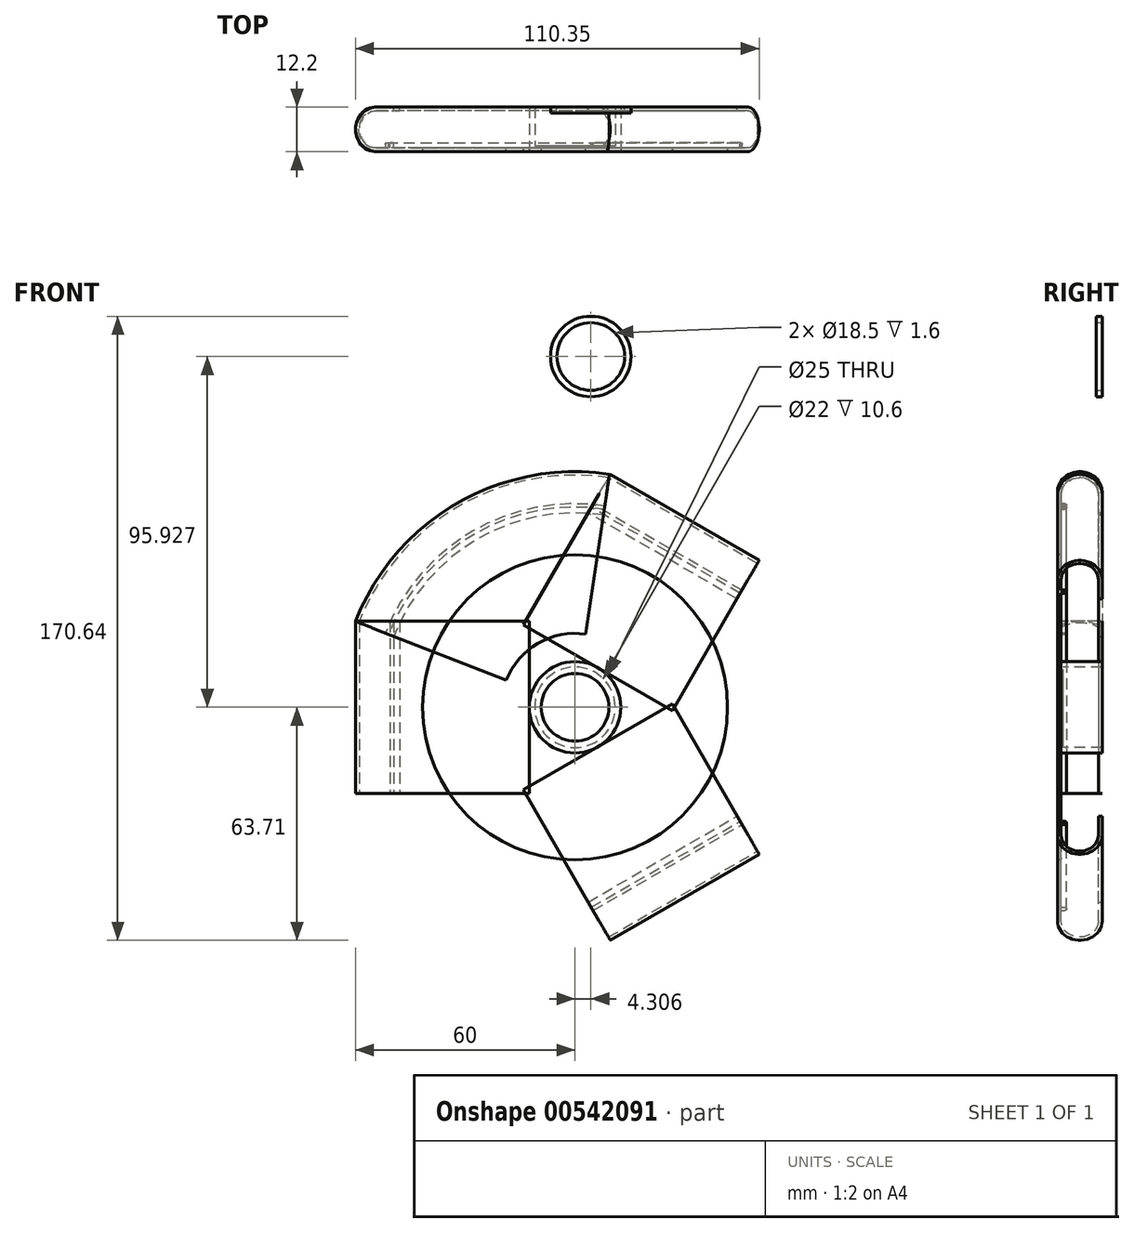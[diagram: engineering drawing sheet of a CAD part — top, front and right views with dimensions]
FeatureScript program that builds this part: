
annotation { "Feature Type Name" : "Feature", "Feature Type Description" : "" }
export const myFeature = defineFeature(function(context is Context, id is Id, definition is map)
    precondition{}
    {
        {
            var Q0;
            Q0=qCreatedBy(makeId("Front.planeOp"),FACE);
            var sketch = newSketch(context, id + "F0", { "sketchPlane" : qUnion([Q0])});
            skCircle(sketch, "E0", {"center": v(0, 0) * mm, "radius": 11 * mm});
            skCircle(sketch, "E1", {"center": v(0, 0) * mm, "radius": 12.5 * mm});
            skLineSegment(sketch, "E2.0", {"start": v(9.65, 63.71) * mm, "end": v(50.35, 40.21) * mm});
            skLineSegment(sketch, "E2.2", {"start": v(50.35, -40.21) * mm, "end": v(9.65, -63.71) * mm});
            skLineSegment(sketch, "E2.4", {"start": v(-60, -23.5) * mm, "end": v(-60, 23.5) * mm});
            skLineSegment(sketch, "E3", {"start": v(-6.25, -10.83) * mm, "end": v(-34.64, -60) * mm, "construction": true});
            skLineSegment(sketch, "E4", {"start": v(12.5, 0) * mm, "end": v(69.28, 0) * mm, "construction": true});
            skLineSegment(sketch, "E5", {"start": v(-6.25, 10.83) * mm, "end": v(-34.64, 60) * mm, "construction": true});
            skPoint(sketch, "E6", {"position": v(30, -51.96) * mm});
            skPoint(sketch, "E7", {"position": v(9.65, -63.71) * mm});
            skPoint(sketch, "E8", {"position": v(50.35, -40.21) * mm});
            skPoint(sketch, "E9", {"position": v(30, 51.96) * mm});
            skPoint(sketch, "E10", {"position": v(9.65, 63.71) * mm});
            skPoint(sketch, "E11", {"position": v(50.35, 40.21) * mm});
            skPoint(sketch, "E12", {"position": v(-60, 0) * mm});
            skPoint(sketch, "E13", {"position": v(-60, 23.5) * mm});
            skPoint(sketch, "E14", {"position": v(-60, -23.5) * mm});
            skLineSegment(sketch, "E15", {"start": v(0, 0) * mm, "end": v(4.62, 8.01) * mm, "construction": true});
            skLineSegment(sketch, "E16", {"start": v(0, 0) * mm, "end": v(-9.25, 0) * mm, "construction": true});
            skLineSegment(sketch, "E17", {"start": v(0, 0) * mm, "end": v(4.62, -8.01) * mm, "construction": true});
            skLineSegment(sketch, "E18", {"start": v(0, 0) * mm, "end": v(1.39, 9.15) * mm, "construction": true});
            skLineSegment(sketch, "E19", {"start": v(0, 0) * mm, "end": v(7.23, 5.77) * mm, "construction": true});
            skLineSegment(sketch, "E20", {"start": v(0, 0) * mm, "end": v(-8.61, 3.37) * mm, "construction": true});
            skLineSegment(sketch, "E21", {"start": v(0, 0) * mm, "end": v(-8.61, -3.37) * mm, "construction": true});
            skLineSegment(sketch, "E22", {"start": v(0, 0) * mm, "end": v(1.39, -9.15) * mm, "construction": true});
            skLineSegment(sketch, "E23", {"start": v(0, 0) * mm, "end": v(7.23, -5.77) * mm, "construction": true});
            skCircle(sketch, "E24", {"center": v(0, 0) * mm, "radius": 9.25 * mm});
            skLineSegment(sketch, "E25.trimOffspring", {"start": v(5.5, 9.53) * mm, "end": v(6.25, 10.83) * mm, "construction": true});
            skLineSegment(sketch, "E26.trimOffspring", {"start": v(1.65, 10.88) * mm, "end": v(9.65, 63.71) * mm, "construction": true});
            skLineSegment(sketch, "E27.trimOffspring", {"start": v(8.6, 6.86) * mm, "end": v(50.35, 40.21) * mm, "construction": true});
            skLineSegment(sketch, "E28.trimOffspring", {"start": v(8.6, -6.86) * mm, "end": v(50.35, -40.21) * mm, "construction": true});
            skLineSegment(sketch, "E29.trimOffspring", {"start": v(5.5, -9.53) * mm, "end": v(6.25, -10.83) * mm, "construction": true});
            skLineSegment(sketch, "E30.trimOffspring", {"start": v(1.65, -10.88) * mm, "end": v(9.65, -63.71) * mm, "construction": true});
            skLineSegment(sketch, "E31.trimOffspring", {"start": v(-10.24, -4.01) * mm, "end": v(-60, -23.5) * mm, "construction": true});
            skLineSegment(sketch, "E32.trimOffspring", {"start": v(-11, 0) * mm, "end": v(-12.5, 0) * mm, "construction": true});
            skLineSegment(sketch, "E33.trimOffspring", {"start": v(-10.24, 4.01) * mm, "end": v(-60, 23.5) * mm, "construction": true});
            skCircle(sketch, "E34", {"center": v(0, 0) * mm, "radius": 20.56 * mm});
            skCircle(sketch, "E35", {"center": v(0, 0) * mm, "radius": 41.68 * mm});
            skSolve(sketch);
        }
        {
            var Q0;
            Q0=makeQuery(id+"F0.imprint","IMPRINT",FACE,{"disambiguationData":[TD([[makeQuery(id+"F0.imprint","IMPRINT",EDGE,{"derivedFrom":sQuery(id+"F0.wireOp",EDGE,"E0")}),-1.0]])]});
            extrude(context, id + "F1", {"entities" : qUnion([Q0]), "oppositeDirection" : true, "depth" : 12.2 * mm, "offsetDistance" : 25 * mm});
        }
        {
            var Q0;
            Q0=qCreatedBy(makeId("Top.planeOp"),FACE);
            var sketch = newSketch(context, id + "F2", { "sketchPlane" : qUnion([Q0])});
            skArc(sketch, "E36", {"start": v(-53.9, 11.2) * mm, "mid": v(-59, 6.1) * mm, "end": v(-53.9, 1) * mm});
            skArc(sketch, "E37", {"start": v(-53.9, 12.2) * mm, "mid": v(-60, 6.1) * mm, "end": v(-53.9, 0) * mm});
            skLineSegment(sketch, "E38", {"start": v(-53.9, 6.1) * mm, "end": v(-53.9, 11.2) * mm, "construction": true});
            skLineSegment(sketch, "E39", {"start": v(-53.9, 6.1) * mm, "end": v(-53.9, 1) * mm, "construction": true});
            skLineSegment(sketch, "E40", {"start": v(-53.9, 0) * mm, "end": v(-49.58, 0) * mm});
            skLineSegment(sketch, "E41", {"start": v(-53.9, 1) * mm, "end": v(-50.58, 1) * mm});
            skPoint(sketch, "E42", {"position": v(-50.58, 1) * mm});
            skLineSegment(sketch, "E43.left", {"start": v(-50.58, 1) * mm, "end": v(-50.58, 2) * mm});
            skLineSegment(sketch, "E43.right", {"start": v(-49.58, 1) * mm, "end": v(-49.58, 2) * mm});
            skCircle(sketch, "E44", {"center": v(-53.9, 6.1) * mm, "radius": 5.1 * mm, "construction": true});
            skArc(sketch, "E45", {"start": v(-49.58, 2) * mm, "mid": v(-50.08, 2.5) * mm, "end": v(-50.58, 2) * mm});
            skLineSegment(sketch, "E46", {"start": v(0, 1) * mm, "end": v(0, 26.09) * mm, "construction": true});
            skLineSegment(sketch, "E47", {"start": v(0, 0) * mm, "end": v(0, -37.62) * mm, "construction": true});
            skPoint(sketch, "E48", {"position": v(-49.58, 1) * mm});
            skPoint(sketch, "E49", {"position": v(-49.58, 0) * mm});
            skLineSegment(sketch, "E50", {"start": v(0, 0) * mm, "end": v(-49.58, 0) * mm});
            skLineSegment(sketch, "E51", {"start": v(-49.58, 1) * mm, "end": v(-12.5, 1) * mm});
            skLineSegment(sketch, "E52", {"start": v(0, 1) * mm, "end": v(0, 0) * mm});
            skLineSegment(sketch, "E53", {"start": v(-53.9, 11.2) * mm, "end": v(-47.9, 11.2) * mm});
            skLineSegment(sketch, "E54", {"start": v(-47.9, 11.2) * mm, "end": v(-47.9, 12.2) * mm});
            skLineSegment(sketch, "E55", {"start": v(-47.9, 12.2) * mm, "end": v(-53.9, 12.2) * mm});
            skPoint(sketch, "E56.start.orphan", {"position": v(-60, 6.1) * mm});
            skLineSegment(sketch, "E57.0", {"start": v(12.5, 0) * mm, "end": v(-12.5, 0) * mm});
            skLineSegment(sketch, "E58", {"start": v(-53.9, 0) * mm, "end": v(-12.5, 0) * mm});
            skPoint(sketch, "E59", {"position": v(-12.5, 1) * mm});
            skPoint(sketch, "E60", {"position": v(-12.5, 0) * mm});
            skLineSegment(sketch, "E61", {"start": v(-12.5, 0) * mm, "end": v(-12.5, 1) * mm});
            skSolve(sketch);
        }
        {
            var Q0;
            Q0=makeQuery(id+"F2.imprint","IMPRINT",FACE,{"disambiguationData":[TD([[makeQuery(id+"F2.imprint","IMPRINT",EDGE,{"derivedFrom":sQuery(id+"F2.wireOp",EDGE,"E36")}),-1.0]])]});
            extrude(context, id + "F3", {"entities" : qUnion([Q0]), "endBound" : BoundingType.SYMMETRIC, "depth" : 47 * mm, "offsetDistance" : 25 * mm});
        }
        {
            var Q0;
            Q0=sQuery(id+"F0.wireOp",EDGE,"E2.2");
            cPoint(context, id + "F4", {"entities" : qUnion([Q0]), "parameter" : 0.5});
        }
        {
            var Q0;
            Q0=sQuery(id+"F0.wireOp",EDGE,"E2.2");
            var Q1;
            Q1=qCreatedBy(id+"F4",VERTEX);
            cPlane(context, id + "F5", {"entities" : qUnion([Q0, Q1]), "cplaneType" : CPlaneType.LINE_POINT, "offset" : 25 * mm, "width" : 150 * mm, "height" : 150 * mm});
        }
        {
            var Q0;
            Q0=qCreatedBy(id+"F5.planeOp",FACE);
            var sketch = newSketch(context, id + "F6", { "sketchPlane" : qUnion([Q0])});
            skArc(sketch, "E62", {"start": v(-11.2, -53.9) * mm, "mid": v(-6.1, -59) * mm, "end": v(-1, -53.9) * mm});
            skArc(sketch, "E63", {"start": v(-12.2, -53.9) * mm, "mid": v(-6.1, -60) * mm, "end": v(0, -53.9) * mm});
            skLineSegment(sketch, "E64", {"start": v(-6.1, -53.9) * mm, "end": v(-11.2, -53.9) * mm, "construction": true});
            skLineSegment(sketch, "E65", {"start": v(-6.1, -53.9) * mm, "end": v(-1, -53.9) * mm, "construction": true});
            skLineSegment(sketch, "E66", {"start": v(0, -53.9) * mm, "end": v(0, -49.58) * mm});
            skLineSegment(sketch, "E67", {"start": v(-1, -53.9) * mm, "end": v(-1, -50.58) * mm});
            skPoint(sketch, "E68", {"position": v(-1, -50.58) * mm});
            skLineSegment(sketch, "E69.left", {"start": v(-1, -50.58) * mm, "end": v(-2, -50.58) * mm});
            skLineSegment(sketch, "E69.right", {"start": v(-1, -49.58) * mm, "end": v(-2, -49.58) * mm});
            skCircle(sketch, "E70", {"center": v(-6.1, -53.9) * mm, "radius": 5.1 * mm, "construction": true});
            skArc(sketch, "E71", {"start": v(-2, -49.58) * mm, "mid": v(-2.5, -50.08) * mm, "end": v(-2, -50.58) * mm});
            skPoint(sketch, "E72", {"position": v(-1, -49.58) * mm});
            skPoint(sketch, "E73", {"position": v(0, -49.58) * mm});
            skLineSegment(sketch, "E74", {"start": v(0, 0) * mm, "end": v(0, -49.58) * mm});
            skLineSegment(sketch, "E75", {"start": v(-1, -49.58) * mm, "end": v(-1, -12.5) * mm});
            skLineSegment(sketch, "E76", {"start": v(-11.2, -53.9) * mm, "end": v(-11.2, -47.9) * mm});
            skLineSegment(sketch, "E77", {"start": v(-11.2, -47.9) * mm, "end": v(-12.2, -47.9) * mm});
            skLineSegment(sketch, "E78", {"start": v(-12.2, -47.9) * mm, "end": v(-12.2, -53.9) * mm});
            skPoint(sketch, "E79.start.orphan", {"position": v(-6.1, -60) * mm});
            skLineSegment(sketch, "E80", {"start": v(-1, -12.5) * mm, "end": v(0, -12.5) * mm});
            skSolve(sketch);
        }
        {
            var Q0;
            Q0=makeQuery(id+"F6.imprint","IMPRINT",FACE,{"disambiguationData":[TD([[makeQuery(id+"F6.imprint","IMPRINT",EDGE,{"derivedFrom":sQuery(id+"F6.wireOp",EDGE,"E62")}),-1.0]])]});
            extrude(context, id + "F7", {"entities" : qUnion([Q0]), "endBound" : BoundingType.SYMMETRIC, "depth" : 47 * mm, "offsetDistance" : 25 * mm});
        }
        {
            var Q0;
            Q0=sQuery(id+"F0.wireOp",EDGE,"E2.0");
            cPoint(context, id + "F8", {"entities" : qUnion([Q0]), "parameter" : 0.5});
        }
        {
            var Q0;
            Q0=sQuery(id+"F0.wireOp",EDGE,"E2.0");
            var Q1;
            Q1=qCreatedBy(id+"F8",VERTEX);
            cPlane(context, id + "F9", {"entities" : qUnion([Q0, Q1]), "cplaneType" : CPlaneType.LINE_POINT, "offset" : 25 * mm, "width" : 150 * mm, "height" : 150 * mm});
        }
        {
            var Q0;
            Q0=qCreatedBy(id+"F9.planeOp",FACE);
            var sketch = newSketch(context, id + "F10", { "sketchPlane" : qUnion([Q0])});
            skArc(sketch, "E81", {"start": v(11.2, 53.85) * mm, "mid": v(6.1, 58.95) * mm, "end": v(1, 53.85) * mm});
            skArc(sketch, "E82", {"start": v(12.2, 53.85) * mm, "mid": v(6.1, 59.95) * mm, "end": v(0, 53.85) * mm});
            skLineSegment(sketch, "E83", {"start": v(6.1, 53.85) * mm, "end": v(11.2, 53.85) * mm, "construction": true});
            skLineSegment(sketch, "E84", {"start": v(6.1, 53.85) * mm, "end": v(1, 53.85) * mm, "construction": true});
            skLineSegment(sketch, "E85", {"start": v(0, 53.85) * mm, "end": v(0, 49.53) * mm});
            skLineSegment(sketch, "E86", {"start": v(1, 53.85) * mm, "end": v(1, 50.53) * mm});
            skPoint(sketch, "E87", {"position": v(1, 50.53) * mm});
            skLineSegment(sketch, "E88.left", {"start": v(1, 50.53) * mm, "end": v(2, 50.53) * mm});
            skLineSegment(sketch, "E88.right", {"start": v(1, 49.53) * mm, "end": v(2, 49.53) * mm});
            skCircle(sketch, "E89", {"center": v(6.1, 53.85) * mm, "radius": 5.1 * mm, "construction": true});
            skArc(sketch, "E90", {"start": v(2, 49.53) * mm, "mid": v(2.5, 50.03) * mm, "end": v(2, 50.53) * mm});
            skPoint(sketch, "E91", {"position": v(1, 49.53) * mm});
            skPoint(sketch, "E92", {"position": v(0, 49.53) * mm});
            skLineSegment(sketch, "E93", {"start": v(0, -0.05) * mm, "end": v(0, 49.53) * mm});
            skLineSegment(sketch, "E94", {"start": v(1, 49.53) * mm, "end": v(1, 12.5) * mm});
            skLineSegment(sketch, "E95", {"start": v(11.2, 53.85) * mm, "end": v(11.2, 47.85) * mm});
            skLineSegment(sketch, "E96", {"start": v(11.2, 47.85) * mm, "end": v(12.2, 47.85) * mm});
            skLineSegment(sketch, "E97", {"start": v(12.2, 47.85) * mm, "end": v(12.2, 53.85) * mm});
            skPoint(sketch, "E98.start.orphan", {"position": v(6.1, 59.95) * mm});
            skLineSegment(sketch, "E99.0", {"start": v(0, -12.5) * mm, "end": v(0, 12.5) * mm});
            skLineSegment(sketch, "E100", {"start": v(0, 12.5) * mm, "end": v(1, 12.5) * mm});
            skSolve(sketch);
        }
        {
            var Q0;
            Q0=makeQuery(id+"F10.imprint","IMPRINT",FACE,{"disambiguationData":[TD([[makeQuery(id+"F10.imprint","IMPRINT",EDGE,{"derivedFrom":sQuery(id+"F10.wireOp",EDGE,"E81")}),-1.0]])]});
            extrude(context, id + "F11", {"entities" : qUnion([Q0]), "endBound" : BoundingType.SYMMETRIC, "depth" : 47 * mm, "offsetDistance" : 25 * mm});
        }
        {
            var Q0;
            Q0=qCreatedBy(makeId("Front.planeOp"),FACE);
            cPlane(context, id + "F12", {"entities" : qUnion([Q0]), "cplaneType" : CPlaneType.OFFSET, "offset" : 12.2 * mm, "oppositeDirection" : true, "width" : 150 * mm, "height" : 150 * mm});
        }
        {
            var Q0;
            Q0=qCreatedBy(id+"F12.planeOp",FACE);
            var sketch = newSketch(context, id + "F13", { "sketchPlane" : qUnion([Q0])});
            skCircle(sketch, "E101.0", {"center": v(0, 0) * mm, "radius": 11 * mm});
            skCircle(sketch, "E102", {"center": v(4.3, 95.93) * mm, "radius": 11 * mm});
            skCircle(sketch, "E103", {"center": v(4.3, 95.93) * mm, "radius": 9.25 * mm});
            skSolve(sketch);
        }
        {
            var Q0;
            Q0=makeQuery(id+"F13.imprint","IMPRINT",FACE,{"disambiguationData":[TD([[makeQuery(id+"F13.imprint","IMPRINT",EDGE,{"derivedFrom":sQuery(id+"F13.wireOp",EDGE,"E101.0")}),1.0]])]});
            extrude(context, id + "F14", {"entities" : qUnion([Q0]), "operationType" : NewBodyOperationType.REMOVE, "depth" : 25 * mm, "offsetDistance" : 25 * mm});
        }
        {
            var Q0;
            Q0=makeQuery(id+"F0.imprint","IMPRINT",FACE,{"disambiguationData":[TD([[makeQuery(id+"F0.imprint","IMPRINT",EDGE,{"derivedFrom":sQuery(id+"F0.wireOp",EDGE,"E0")}),1.0]])]});
            extrude(context, id + "F15", {"entities" : qUnion([Q0]), "operationType" : NewBodyOperationType.ADD, "oppositeDirection" : true, "depth" : 1.6 * mm, "offsetDistance" : 25 * mm});
        }
        {
            var Q0;
            Q0=sQuery(id+"F0.wireOp",EDGE,"E18");
            var Q1;
            Q1=sQuery(id+"F0.wireOp",VERTEX,"E5.end");
            cPlane(context, id + "F16", {"entities" : qUnion([Q0, Q1]), "cplaneType" : CPlaneType.LINE_ANGLE, "offset" : 25 * mm, "angle" : 90 * degree, "width" : 150 * mm, "height" : 150 * mm});
        }
        {
            var Q0;
            Q0=qCreatedBy(id+"F16.planeOp",FACE);
            var sketch = newSketch(context, id + "F17", { "sketchPlane" : qUnion([Q0])});
            skLineSegment(sketch, "E104.0.0", {"start": v(0, 20.2) * mm, "end": v(0, 58.7) * mm});
            skEllipticalArc(sketch, "E104.0.1", {});
            skLineSegment(sketch, "E104.0.2", {"start": v(12.2, 58.7) * mm, "end": v(12.2, 53.12) * mm});
            skLineSegment(sketch, "E104.0.3", {"start": v(12.2, 53.12) * mm, "end": v(11.2, 53.12) * mm});
            skLineSegment(sketch, "E104.0.4", {"start": v(11.2, 53.12) * mm, "end": v(11.2, 58.7) * mm});
            skEllipticalArc(sketch, "E104.0.5", {});
            skLineSegment(sketch, "E104.0.6", {"start": v(1, 58.7) * mm, "end": v(1, 55.62) * mm});
            skLineSegment(sketch, "E104.0.7", {"start": v(1, 55.62) * mm, "end": v(2, 55.62) * mm});
            skEllipticalArc(sketch, "E104.0.8", {});
            skLineSegment(sketch, "E104.0.9", {"start": v(2, 54.68) * mm, "end": v(1, 54.68) * mm});
            skLineSegment(sketch, "E104.0.10", {"start": v(1, 54.68) * mm, "end": v(1, 20.2) * mm});
            skLineSegment(sketch, "E104.0.11", {"start": v(1, 20.2) * mm, "end": v(0, 20.2) * mm});
            skPoint(sketch, "E105", {"position": v(6.1, 64.39) * mm});
            const initialGuessF17  = {"E104.0.1": [0.0061, 0.05870712344844824, 1, 0, 0.0061, 0.005679882329674195, 0, 3.141592653589793], "E104.0.5": [0.0061, 0.058707123448448244, -1, 0, 0.0051, 0.004748754078907933, 3.141592653589793, 0], "E104.0.8": [0.002, 0.05515020930713565, 1, 0, 0.0005, 0.00046556412538313114, 4.71238898038469, 1.5707963267948966]};
            skSetInitialGuess(sketch, initialGuessF17);
            skSolve(sketch);
        }
        {
            var Q0;
            Q0=sQuery(id+"F0.wireOp",EDGE,"E20");
            var Q1;
            Q1=sQuery(id+"F0.wireOp",VERTEX,"E5.end");
            cPlane(context, id + "F18", {"entities" : qUnion([Q0, Q1]), "cplaneType" : CPlaneType.LINE_ANGLE, "offset" : 25 * mm, "angle" : 90 * degree, "width" : 150 * mm, "height" : 150 * mm});
        }
        {
            var Q0;
            Q0=qCreatedBy(id+"F18.planeOp",FACE);
            var sketch = newSketch(context, id + "F19", { "sketchPlane" : qUnion([Q0])});
            skLineSegment(sketch, "E106.0.0", {"start": v(-58.76, 0) * mm, "end": v(-20.2, 0) * mm});
            skLineSegment(sketch, "E106.0.1", {"start": v(-20.2, 0) * mm, "end": v(-20.2, -1) * mm});
            skLineSegment(sketch, "E106.0.2", {"start": v(-20.2, -1) * mm, "end": v(-54.74, -1) * mm});
            skLineSegment(sketch, "E106.0.3", {"start": v(-54.74, -1) * mm, "end": v(-54.74, -2) * mm});
            skEllipticalArc(sketch, "E106.0.4", {});
            skLineSegment(sketch, "E106.0.5", {"start": v(-55.67, -2) * mm, "end": v(-55.67, -1) * mm});
            skLineSegment(sketch, "E106.0.6", {"start": v(-55.67, -1) * mm, "end": v(-58.76, -1) * mm});
            skEllipticalArc(sketch, "E106.0.7", {});
            skLineSegment(sketch, "E106.0.8", {"start": v(-58.76, -11.2) * mm, "end": v(-53.17, -11.2) * mm});
            skLineSegment(sketch, "E106.0.9", {"start": v(-53.17, -11.2) * mm, "end": v(-53.17, -12.2) * mm});
            skLineSegment(sketch, "E106.0.10", {"start": v(-53.17, -12.2) * mm, "end": v(-58.76, -12.2) * mm});
            skEllipticalArc(sketch, "E106.0.11", {});
            skPoint(sketch, "E107", {"position": v(-64.44, -6.1) * mm});
            const initialGuessF19  = {"E106.0.4": [-0.055201162406468836, -0.002, 0, 1, 0.0005, 0.00046556412538313114, 1.5707963267948966, 4.71238898038469], "E106.0.7": [-0.058758076547781424, -0.0061, 0, -1, 0.0051, 0.004748754078907933, 3.141592653589793, 0], "E106.0.11": [-0.058758076547781424, -0.0061, 0, 1, 0.0061, 0.005679882329674194, 0, 3.141592653589793]};
            skSetInitialGuess(sketch, initialGuessF19);
            skSolve(sketch);
        }
        {
            var Q0;
            Q0 = qSketchRegion(id + "F19", true);
            var Q1;
            Q1=sQuery(id+"F2.wireOp",EDGE,"E47");
            revolve(context, id + "F20", {"entities" : qUnion([Q0]), "axis" : qUnion([Q1]), "revolveType" : RevolveType.ONE_DIRECTION, "oppositeDirection" : true, "angle" : 77 * degree});
        }
        {
            var Q0;
            Q0=qCreatedBy(makeId("Front.planeOp"),FACE);
            cPlane(context, id + "F21", {"entities" : qUnion([Q0]), "cplaneType" : CPlaneType.OFFSET, "offset" : 6.1 * mm, "oppositeDirection" : true, "width" : 150 * mm, "height" : 150 * mm});
        }
        {
            var Q0;
            Q0=makeQuery(id+"F13.imprint","IMPRINT",FACE,{"disambiguationData":[TD([[makeQuery(id+"F13.imprint","IMPRINT",EDGE,{"derivedFrom":sQuery(id+"F13.wireOp",EDGE,"E102")}),1.0]])]});
            extrude(context, id + "F22", {"entities" : qUnion([Q0]), "depth" : 1.6 * mm, "offsetDistance" : 25 * mm});
        }
        {
            var Q0;
            Q0=makeQuery(id+"F0.imprint","IMPRINT",FACE,{"disambiguationData":[TD([[makeQuery(id+"F0.imprint","IMPRINT",EDGE,{"derivedFrom":sQuery(id+"F0.wireOp",EDGE,"E34")}),-1.0]])]});
            var Q1;
            Q1=makeQuery(id+"F0.imprint","IMPRINT",FACE,{"disambiguationData":[TD([[makeQuery(id+"F0.imprint","IMPRINT",EDGE,{"derivedFrom":sQuery(id+"F0.wireOp",EDGE,"E1")}),-1.0]])]});
            extrude(context, id + "F23", {"entities" : qUnion([Q0, Q1]), "oppositeDirection" : true, "depth" : 1 * mm, "offsetDistance" : 25 * mm});
        }
    });
